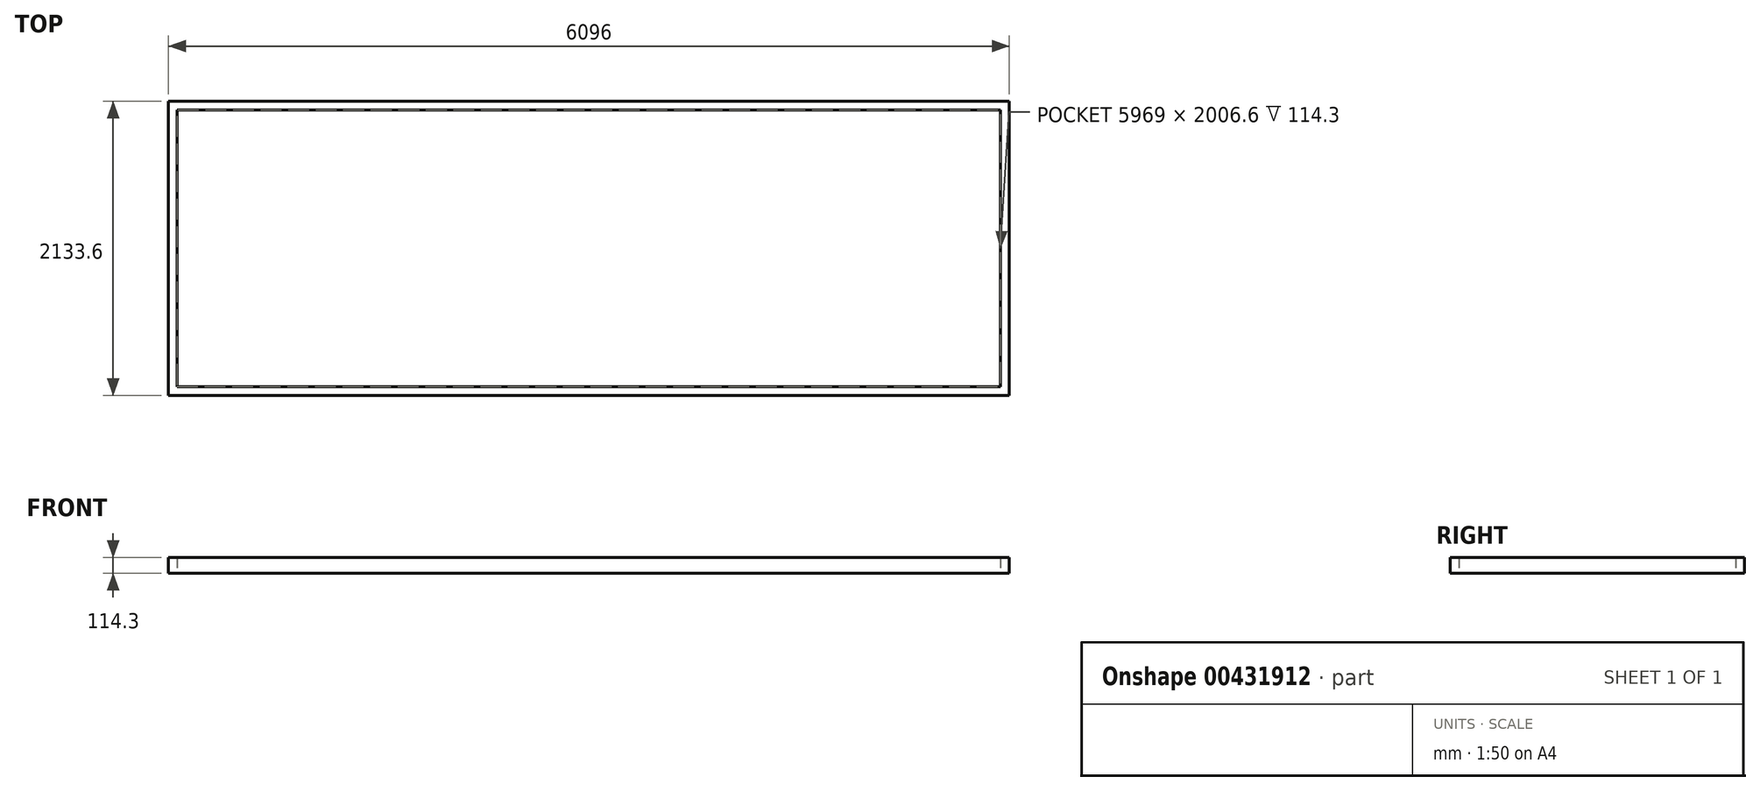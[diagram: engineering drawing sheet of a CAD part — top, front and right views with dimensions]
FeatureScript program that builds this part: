
annotation { "Feature Type Name" : "Feature", "Feature Type Description" : "" }
export const myFeature = defineFeature(function(context is Context, id is Id, definition is map)
    precondition{}
    {
        {
            var Q0;
            Q0=qCreatedBy(makeId("Top.planeOp"),FACE);
            var sketch = newSketch(context, id + "F0", { "sketchPlane" : qUnion([Q0])});
            skLineSegment(sketch, "E0.bottom", {"start": v(5112.37, -1018.57) * mm, "end": v(-983.63, -1018.57) * mm});
            skLineSegment(sketch, "E0.top", {"start": v(5112.37, 1115.03) * mm, "end": v(-983.63, 1115.03) * mm});
            skLineSegment(sketch, "E0.left", {"start": v(5112.37, -1018.57) * mm, "end": v(5112.37, 1115.03) * mm});
            skLineSegment(sketch, "E0.right", {"start": v(-983.63, -1018.57) * mm, "end": v(-983.63, 1115.03) * mm});
            skSolve(sketch);
        }
        {
            var Q0;
            Q0 = qSketchRegion(id + "F0", true);
            var Q1;
            Q1=makeQuery(id+"F0.imprint","IMPRINT",FACE,{"disambiguationData":[TD([[makeQuery(id+"F0.imprint","IMPRINT",EDGE,{"derivedFrom":sQuery(id+"F0.wireOp",EDGE,"E0.bottom")}),-1.0]])]});
            extrude(context, id + "F1", {"entities" : qUnion([Q0, Q1]), "depth" : 1 / 406.4 * mm});
        }
        {
            var Q0;
            Q0=makeQuery(id+"F1.opExtrude","CAP_FACE",FACE,{"disambiguationData":[OSD([sQuery(id+"F0.wireOp",EDGE,"E0.bottom"),sQuery(id+"F0.wireOp",EDGE,"E0.top"),sQuery(id+"F0.wireOp",EDGE,"E0.left"),sQuery(id+"F0.wireOp",EDGE,"E0.right")])],"isStart":false});
            var sketch = newSketch(context, id + "F2", { "sketchPlane" : qUnion([Q0])});
            skLineSegment(sketch, "E1.bottom", {"start": v(5112.37, 1115.03) * mm, "end": v(-983.63, 1115.03) * mm});
            skLineSegment(sketch, "E1.top", {"start": v(5112.37, 1051.53) * mm, "end": v(-983.63, 1051.53) * mm});
            skLineSegment(sketch, "E1.left", {"start": v(5112.37, 1115.03) * mm, "end": v(5112.37, 1051.53) * mm});
            skLineSegment(sketch, "E1.right", {"start": v(-983.63, 1115.03) * mm, "end": v(-983.63, 1051.53) * mm});
            skLineSegment(sketch, "E2.bottom", {"start": v(-983.63, -1018.57) * mm, "end": v(-920.13, -1018.57) * mm});
            skLineSegment(sketch, "E2.top", {"start": v(-983.63, 1115.03) * mm, "end": v(-920.13, 1115.03) * mm});
            skLineSegment(sketch, "E2.left", {"start": v(-983.63, -1018.57) * mm, "end": v(-983.63, 1115.03) * mm});
            skLineSegment(sketch, "E2.right", {"start": v(-920.13, -1018.57) * mm, "end": v(-920.13, 1115.03) * mm});
            skLineSegment(sketch, "E3.bottom", {"start": v(-920.13, -1018.57) * mm, "end": v(-983.63, -1018.57) * mm});
            skLineSegment(sketch, "E3.top", {"start": v(-920.13, -1018.57) * mm, "end": v(-983.63, -1018.57) * mm});
            skLineSegment(sketch, "E3.left", {"start": v(-920.13, -1018.57) * mm, "end": v(-920.13, -1018.57) * mm});
            skLineSegment(sketch, "E3.right", {"start": v(-983.63, -1018.57) * mm, "end": v(-983.63, -1018.57) * mm});
            skLineSegment(sketch, "E4.bottom", {"start": v(-983.63, -1018.57) * mm, "end": v(5112.37, -1018.57) * mm});
            skLineSegment(sketch, "E4.top", {"start": v(-983.63, -955.07) * mm, "end": v(5112.37, -955.07) * mm});
            skLineSegment(sketch, "E4.left", {"start": v(-983.63, -1018.57) * mm, "end": v(-983.63, -955.07) * mm});
            skLineSegment(sketch, "E4.right", {"start": v(5112.37, -1018.57) * mm, "end": v(5112.37, -955.07) * mm});
            skLineSegment(sketch, "E5.bottom", {"start": v(5112.37, -1018.57) * mm, "end": v(5048.87, -1018.57) * mm});
            skLineSegment(sketch, "E5.top", {"start": v(5112.37, 1115.03) * mm, "end": v(5048.87, 1115.03) * mm});
            skLineSegment(sketch, "E5.left", {"start": v(5112.37, -1018.57) * mm, "end": v(5112.37, 1115.03) * mm});
            skLineSegment(sketch, "E5.right", {"start": v(5048.87, -1018.57) * mm, "end": v(5048.87, 1115.03) * mm});
            skSolve(sketch);
        }
        {
            var Q0;
            Q0 = qSketchRegion(id + "F2", true);
            extrude(context, id + "F3", {"entities" : qUnion([Q0]), "operationType" : NewBodyOperationType.ADD, "depth" : 114.3 * mm});
        }
    });
